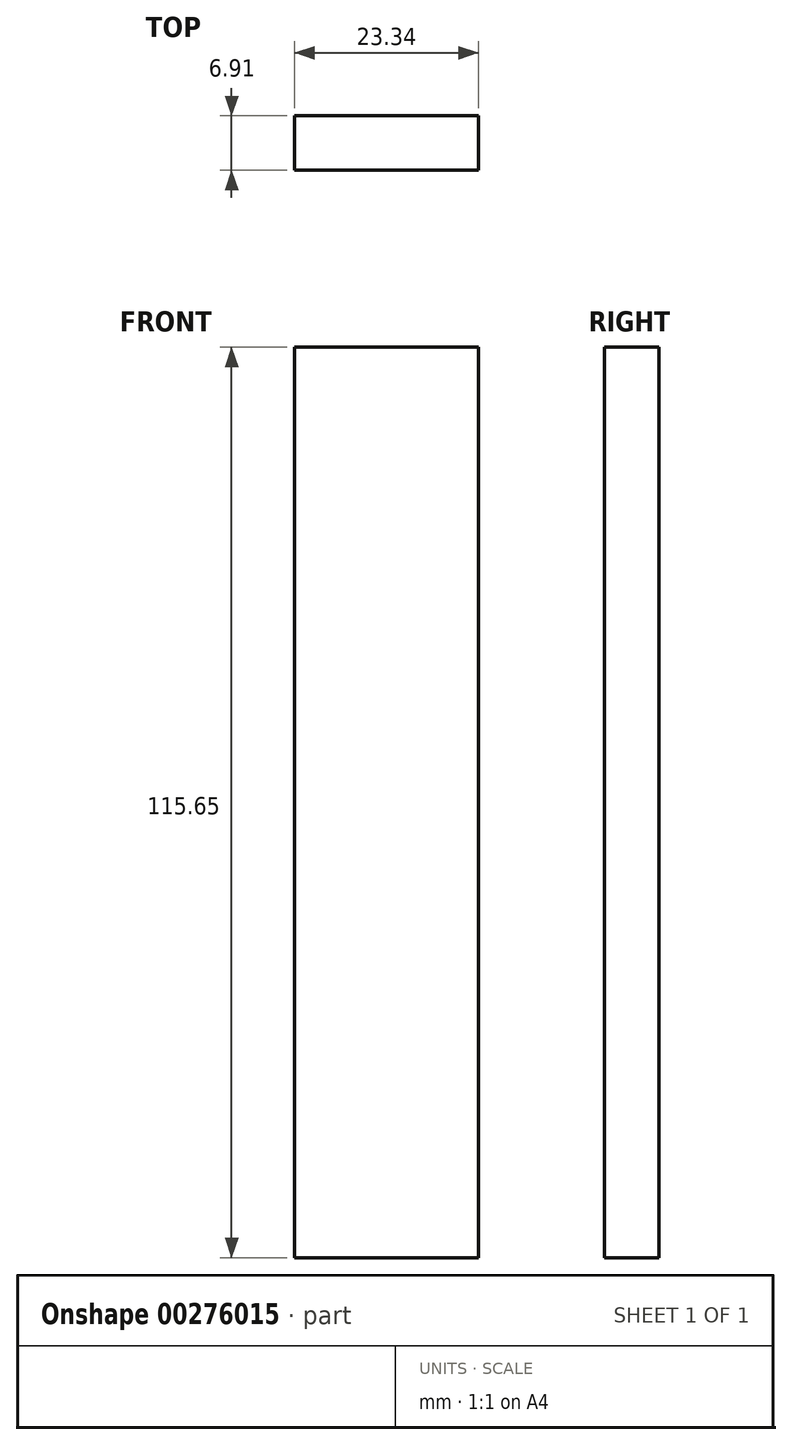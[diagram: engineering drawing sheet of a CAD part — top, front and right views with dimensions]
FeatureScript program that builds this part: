
annotation { "Feature Type Name" : "Feature", "Feature Type Description" : "" }
export const myFeature = defineFeature(function(context is Context, id is Id, definition is map)
    precondition{}
    {
        {
            var Q0;
            Q0=qCreatedBy(makeId("Front.planeOp"),FACE);
            var sketch = newSketch(context, id + "F0", { "sketchPlane" : qUnion([Q0])});
            skLineSegment(sketch, "E0.bottom", {"start": v(-23.34, 50.8) * mm, "end": v(0, 50.8) * mm});
            skLineSegment(sketch, "E0.top", {"start": v(-23.34, -64.86) * mm, "end": v(0, -64.86) * mm});
            skLineSegment(sketch, "E0.left", {"start": v(-23.34, 50.8) * mm, "end": v(-23.34, -64.86) * mm});
            skLineSegment(sketch, "E0.right", {"start": v(0, 50.8) * mm, "end": v(0, -64.86) * mm});
            skSolve(sketch);
        }
        {
            var Q0;
            Q0=makeQuery(id+"F0.imprint","IMPRINT",FACE,{"disambiguationData":[TD([[makeQuery(id+"F0.imprint","IMPRINT",EDGE,{"derivedFrom":sQuery(id+"F0.wireOp",EDGE,"E0.bottom")}),-1.0]])]});
            var Q1;
            Q1=makeQuery(id+"F0.imprint","IMPRINT",FACE,{"disambiguationData":[TD([[makeQuery(id+"F0.imprint","IMPRINT",EDGE,{"derivedFrom":sQuery(id+"F0.wireOp",EDGE,"E0.bottom")}),-1.0]])]});
            extrude(context, id + "F1", {"entities" : qUnion([Q0, Q1]), "depth" : 6.9 * mm});
        }
    });
